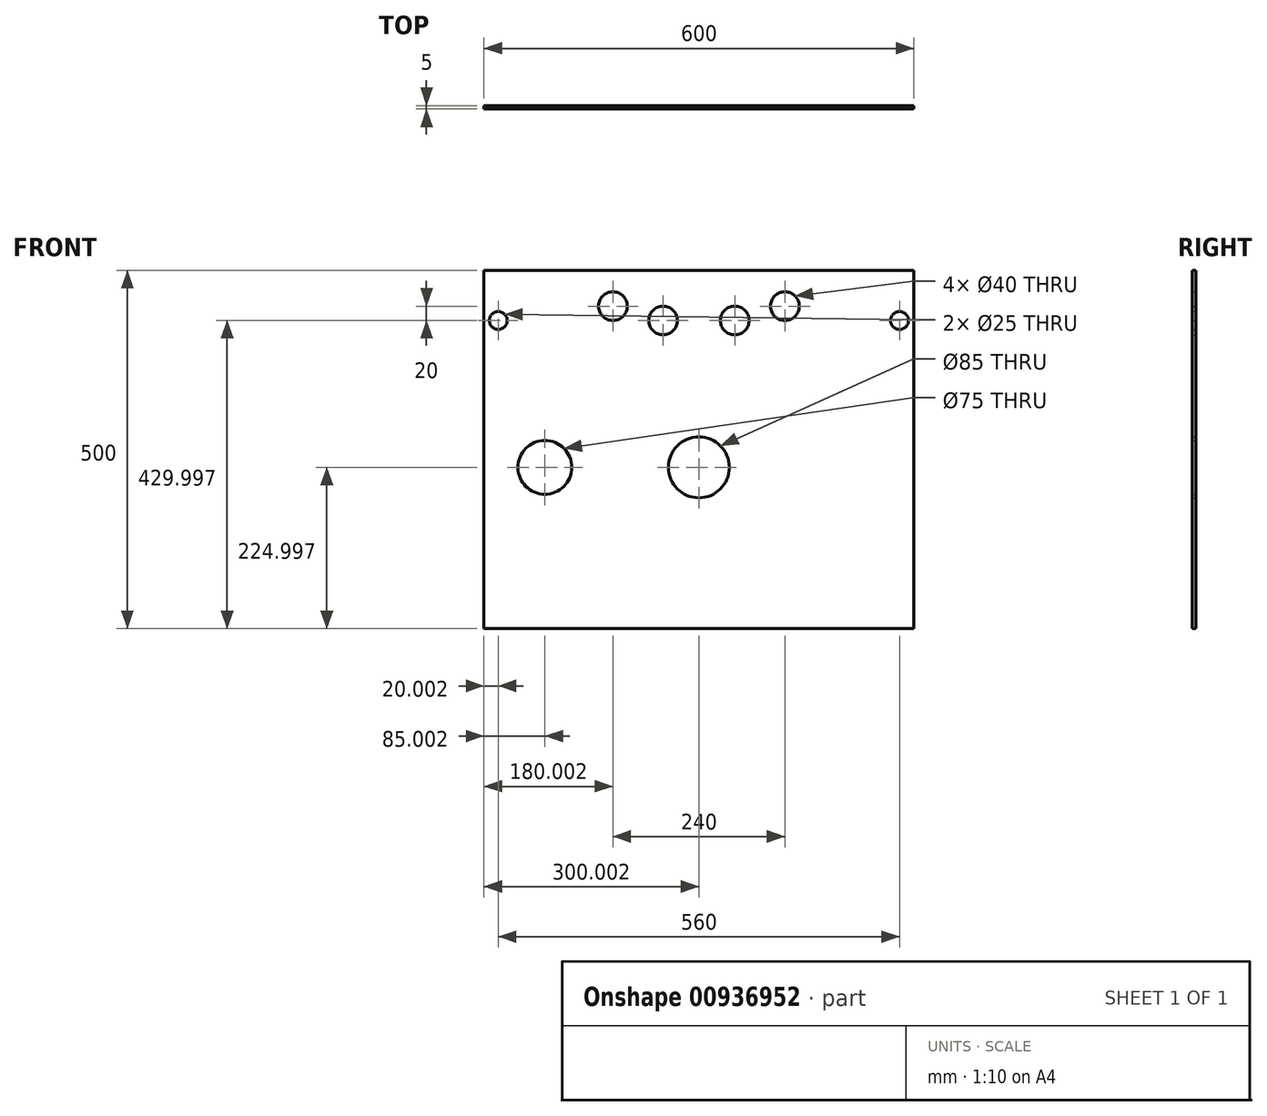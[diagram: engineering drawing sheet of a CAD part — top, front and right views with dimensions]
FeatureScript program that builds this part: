
annotation { "Feature Type Name" : "Feature", "Feature Type Description" : "" }
export const myFeature = defineFeature(function(context is Context, id is Id, definition is map)
    precondition{}
    {
        {
            var Q0;
            Q0=qCreatedBy(makeId("Front.planeOp"),FACE);
            var sketch = newSketch(context, id + "F0", { "sketchPlane" : qUnion([Q0])});
            skLineSegment(sketch, "E0.bottom", {"start": v(59.41, 9.9) * mm, "end": v(-540.59, 9.9) * mm});
            skLineSegment(sketch, "E0.top", {"start": v(59.41, 509.9) * mm, "end": v(-540.59, 509.9) * mm});
            skLineSegment(sketch, "E0.left", {"start": v(59.41, 9.9) * mm, "end": v(59.41, 509.9) * mm});
            skLineSegment(sketch, "E0.right", {"start": v(-540.59, 9.9) * mm, "end": v(-540.59, 509.9) * mm});
            skCircle(sketch, "E1", {"center": v(-360.59, 459.9) * mm, "radius": 20 * mm});
            skCircle(sketch, "E2", {"center": v(-290.59, 439.9) * mm, "radius": 20 * mm});
            skCircle(sketch, "E3", {"center": v(-520.59, 439.9) * mm, "radius": 12.5 * mm});
            skLineSegment(sketch, "E4", {"start": v(-240.59, 9.9) * mm, "end": v(-240.59, 509.9) * mm, "construction": true});
            skCircle(sketch, "E5.MirrorC", {"center": v(-190.59, 439.9) * mm, "radius": 20 * mm});
            skCircle(sketch, "E6.MirrorC", {"center": v(-120.59, 459.9) * mm, "radius": 20 * mm});
            skCircle(sketch, "E7.MirrorC", {"center": v(39.41, 439.9) * mm, "radius": 12.5 * mm});
            skCircle(sketch, "E8", {"center": v(-455.59, 234.9) * mm, "radius": 37.5 * mm});
            skLineSegment(sketch, "E9", {"start": v(-540.59, 369.9) * mm, "end": v(59.41, 369.9) * mm, "construction": true});
            skPoint(sketch, "E10", {"position": v(-456.63, 272.38) * mm});
            skPoint(sketch, "E11", {"position": v(36.8, 427.67) * mm});
            skPoint(sketch, "E12", {"position": v(-517.97, 427.67) * mm});
            skLineSegment(sketch, "E13", {"start": v(-517.97, 427.67) * mm, "end": v(-456.63, 272.38) * mm});
            skLineSegment(sketch, "E14", {"start": v(36.8, 427.67) * mm, "end": v(-456.63, 272.38) * mm});
            skLineSegment(sketch, "E15", {"start": v(-540.59, 49.9) * mm, "end": v(59.41, 49.9) * mm, "construction": true});
            skLineSegment(sketch, "E16", {"start": v(-500.59, 509.9) * mm, "end": v(-500.59, 9.9) * mm, "construction": true});
            skLineSegment(sketch, "E17.MirrorCS", {"start": v(19.41, 509.9) * mm, "end": v(19.41, 9.9) * mm, "construction": true});
            skPoint(sketch, "E18", {"position": v(-299.87, 422.18) * mm});
            skPoint(sketch, "E19", {"position": v(-514.29, 450.7) * mm});
            skLineSegment(sketch, "E20", {"start": v(-514.29, 450.7) * mm, "end": v(-299.87, 422.18) * mm});
            skLineSegment(sketch, "E21.MirrorCS", {"start": v(33.11, 450.7) * mm, "end": v(-181.3, 422.18) * mm});
            skPoint(sketch, "E22", {"position": v(-371.77, 476.48) * mm});
            skPoint(sketch, "E23", {"position": v(-526.89, 450.7) * mm});
            skLineSegment(sketch, "E24", {"start": v(-371.77, 476.48) * mm, "end": v(-526.89, 450.7) * mm});
            skLineSegment(sketch, "E25.MirrorCS", {"start": v(-109.4, 476.48) * mm, "end": v(45.71, 450.7) * mm});
            skLineSegment(sketch, "E26", {"start": v(-540.59, 94.9) * mm, "end": v(59.41, 94.9) * mm, "construction": true});
            skLineSegment(sketch, "E27", {"start": v(-540.59, 164.9) * mm, "end": v(59.41, 164.9) * mm, "construction": true});
            skLineSegment(sketch, "E28", {"start": v(-540.59, 234.9) * mm, "end": v(59.41, 234.9) * mm, "construction": true});
            skLineSegment(sketch, "E29", {"start": v(59.41, 304.9) * mm, "end": v(-540.59, 304.9) * mm, "construction": true});
            skLineSegment(sketch, "E30", {"start": v(-455.59, 9.9) * mm, "end": v(-455.59, 509.9) * mm, "construction": true});
            skLineSegment(sketch, "E31", {"start": v(-385.59, 9.9) * mm, "end": v(-385.59, 509.9) * mm, "construction": true});
            skLineSegment(sketch, "E32", {"start": v(-315.59, 9.9) * mm, "end": v(-315.59, 509.9) * mm, "construction": true});
            skCircle(sketch, "E33", {"center": v(-240.59, 234.9) * mm, "radius": 42.5 * mm});
            skSolve(sketch);
        }
        {
            var Q0;
            Q0=qSketchRegion(id+"F0",true);
            extrude(context, id + "F1", {"entities" : qUnion([Q0]), "depth" : 5 * mm, "offsetDistance" : 25 * mm});
        }
    });
